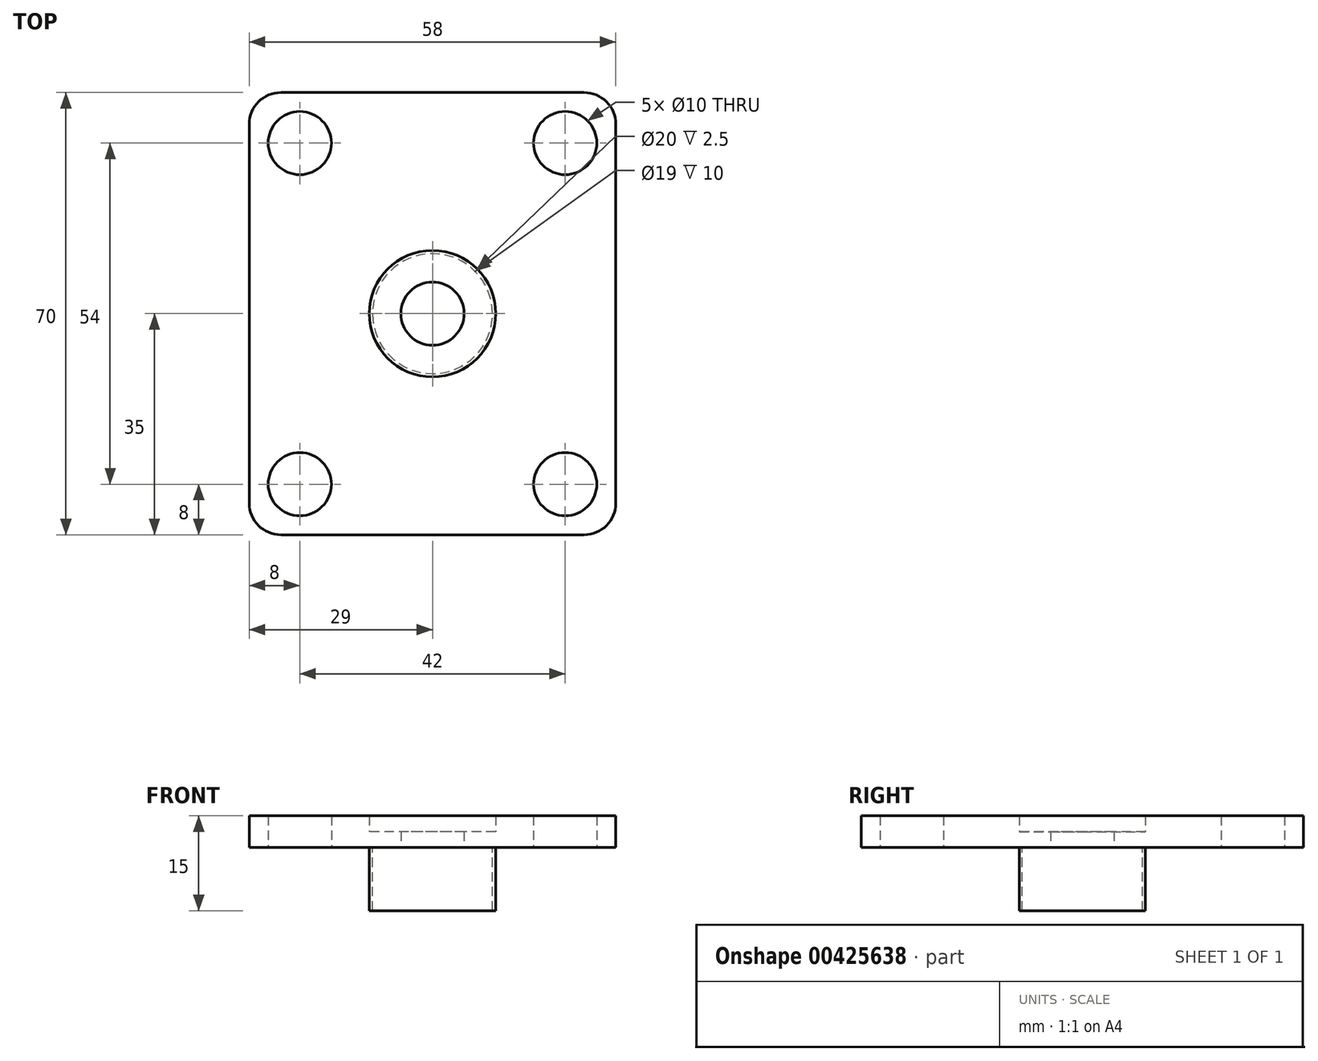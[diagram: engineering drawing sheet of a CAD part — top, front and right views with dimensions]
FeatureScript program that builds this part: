
annotation { "Feature Type Name" : "Feature", "Feature Type Description" : "" }
export const myFeature = defineFeature(function(context is Context, id is Id, definition is map)
    precondition{}
    {
        {
            var Q0;
            Q0=qCreatedBy(makeId("Top.planeOp"),FACE);
            var sketch = newSketch(context, id + "F0", { "sketchPlane" : qUnion([Q0])});
            skLineSegment(sketch, "E0.bottom", {"start": v(29, 35) * mm, "end": v(-29, 35) * mm});
            skLineSegment(sketch, "E0.top", {"start": v(29, -35) * mm, "end": v(-29, -35) * mm});
            skLineSegment(sketch, "E0.left", {"start": v(29, 35) * mm, "end": v(29, -35) * mm});
            skLineSegment(sketch, "E0.right", {"start": v(-29, 35) * mm, "end": v(-29, -35) * mm});
            skPoint(sketch, "E0.middle", {"position": v(0, 0) * mm});
            skLineSegment(sketch, "E1", {"start": v(0, 0) * mm, "end": v(0, 35) * mm, "construction": true});
            skLineSegment(sketch, "E2", {"start": v(0, 0) * mm, "end": v(-29, 0) * mm, "construction": true});
            skLineSegment(sketch, "E3", {"start": v(29, 0) * mm, "end": v(0, 0) * mm, "construction": true});
            skLineSegment(sketch, "E4", {"start": v(0, 0) * mm, "end": v(0, -35) * mm, "construction": true});
            skCircle(sketch, "E5", {"center": v(-21, 27) * mm, "radius": 5 * mm});
            skCircle(sketch, "E6.MirrorC", {"center": v(21, 27) * mm, "radius": 5 * mm});
            skLineSegment(sketch, "E7.MirrorCS", {"start": v(-29, 0) * mm, "end": v(0, 0) * mm, "construction": true});
            skCircle(sketch, "E8.MirrorC", {"center": v(21, -27) * mm, "radius": 5 * mm});
            skCircle(sketch, "E9.MirrorC", {"center": v(-21, -27) * mm, "radius": 5 * mm});
            skCircle(sketch, "E10", {"center": v(0, 0) * mm, "radius": 10 * mm});
            skCircle(sketch, "E11", {"center": v(0, 0) * mm, "radius": 5 * mm});
            skCircle(sketch, "E12", {"center": v(0, 0) * mm, "radius": 9.5 * mm});
            skSolve(sketch);
        }
        {
            var Q0;
            Q0=makeQuery(id+"F0.imprint","IMPRINT",FACE,{"disambiguationData":[TD([[makeQuery(id+"F0.imprint","IMPRINT",EDGE,{"derivedFrom":sQuery(id+"F0.wireOp",EDGE,"E0.bottom")}),1.0]])]});
            extrude(context, id + "F1", {"entities" : qUnion([Q0]), "depth" : 5 * mm});
        }
        {
            var Q0;
            Q0=makeQuery(id+"F0.imprint","IMPRINT",FACE,{"disambiguationData":[TD([[makeQuery(id+"F0.imprint","IMPRINT",EDGE,{"derivedFrom":sQuery(id+"F0.wireOp",EDGE,"E10")}),1.0]])]});
            var Q1;
            Q1=makeQuery(id+"F0.imprint","IMPRINT",FACE,{"disambiguationData":[TD([[makeQuery(id+"F0.imprint","IMPRINT",EDGE,{"derivedFrom":sQuery(id+"F0.wireOp",EDGE,"E11")}),-1.0]])]});
            extrude(context, id + "F2", {"entities" : qUnion([Q0, Q1]), "operationType" : NewBodyOperationType.ADD, "depth" : 2.5 * mm});
        }
        {
            var Q0;
            Q0=makeQuery(id+"F0.imprint","IMPRINT",FACE,{"disambiguationData":[TD([[makeQuery(id+"F0.imprint","IMPRINT",EDGE,{"derivedFrom":sQuery(id+"F0.wireOp",EDGE,"E10")}),1.0]])]});
            extrude(context, id + "F3", {"entities" : qUnion([Q0]), "operationType" : NewBodyOperationType.ADD, "oppositeDirection" : true, "depth" : 10 * mm});
        }
        {
            var Q0;
            Q0=makeQuery(id+"F1.opExtrude","SWEPT_EDGE",EDGE,{"disambiguationData":[OSD([sQuery(id+"F0.wireOp",EDGE,"E0.top"),sQuery(id+"F0.wireOp",EDGE,"E0.right")])]});
            var Q1;
            Q1=makeQuery(id+"F1.opExtrude","SWEPT_EDGE",EDGE,{"disambiguationData":[OSD([sQuery(id+"F0.wireOp",EDGE,"E0.top"),sQuery(id+"F0.wireOp",EDGE,"E0.left")])]});
            var Q2;
            Q2=makeQuery(id+"F1.opExtrude","SWEPT_EDGE",EDGE,{"disambiguationData":[OSD([sQuery(id+"F0.wireOp",EDGE,"E0.bottom"),sQuery(id+"F0.wireOp",EDGE,"E0.left")])]});
            var Q3;
            Q3=makeQuery(id+"F1.opExtrude","SWEPT_EDGE",EDGE,{"disambiguationData":[OSD([sQuery(id+"F0.wireOp",EDGE,"E0.bottom"),sQuery(id+"F0.wireOp",EDGE,"E0.right")])]});
            fillet(context, id + "F4", {"entities" : qUnion([Q0, Q1, Q2, Q3]), "radius" : 5 * mm, "tangentPropagation" : true, "allowEdgeOverflow" : false});
        }
    });
